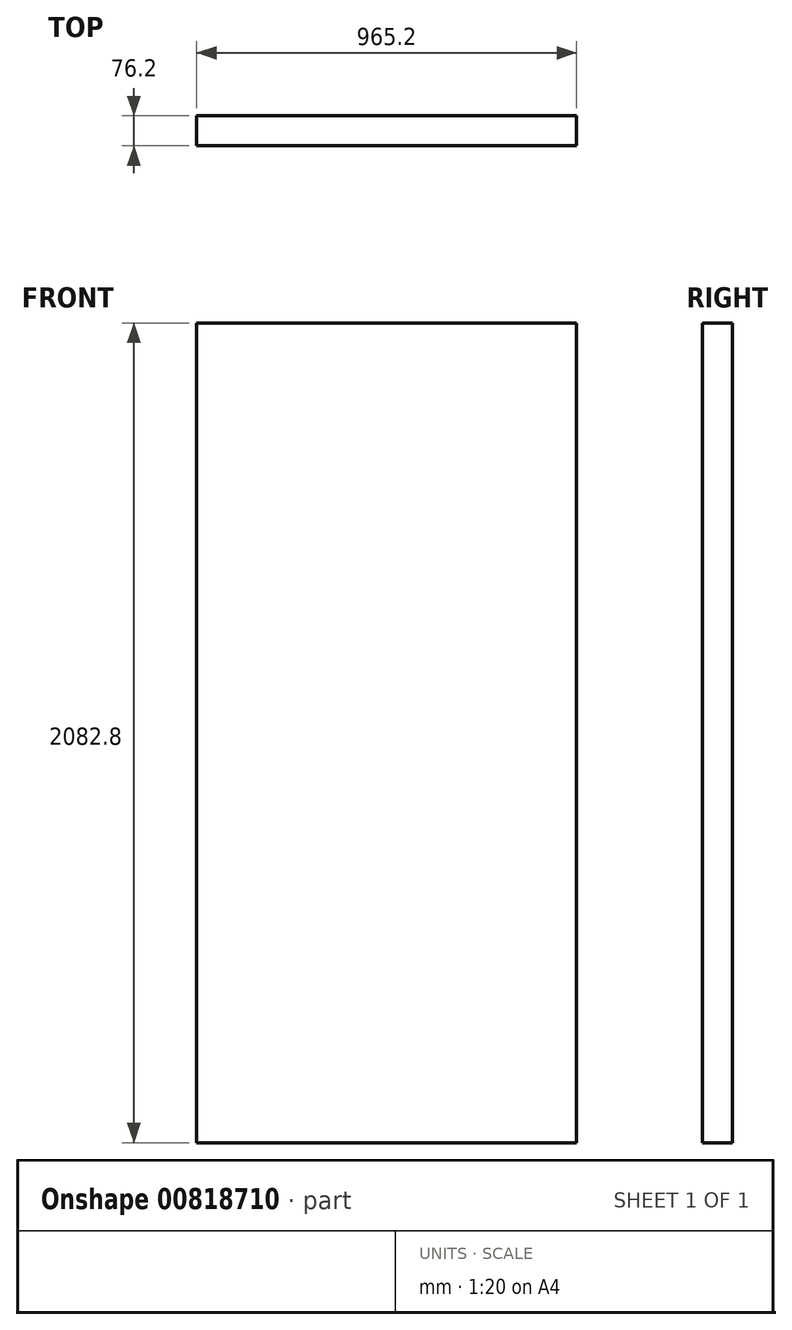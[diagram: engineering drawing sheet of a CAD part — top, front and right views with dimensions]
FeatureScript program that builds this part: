
annotation { "Feature Type Name" : "Feature", "Feature Type Description" : "" }
export const myFeature = defineFeature(function(context is Context, id is Id, definition is map)
    precondition{}
    {
        {
            var Q0;
            Q0=qCreatedBy(makeId("Front.planeOp"), FACE);
            var sketch = newSketch(context, id + "F0", { "sketchPlane" : qUnion([Q0])});
            skLineSegment(sketch, "E0.bottom", {"start": v(965.2, 2082.8) * mm, "end": v(0, 2082.8) * mm});
            skLineSegment(sketch, "E0.top", {"start": v(965.2, 0) * mm, "end": v(0, 0) * mm});
            skLineSegment(sketch, "E0.left", {"start": v(965.2, 2082.8) * mm, "end": v(965.2, 0) * mm});
            skLineSegment(sketch, "E0.right", {"start": v(0, 2082.8) * mm, "end": v(0, 0) * mm});
            skSolve(sketch);
        }
        {
            var Q0;
            Q0 = qSketchRegion(id + "F0", true);
            extrude(context, id + "F1", {"entities" : qUnion([Q0]), "domain" : OperationDomain.MODEL, "flatOperationType" : FlatOperationType.REMOVE, "depth" : 76.2 * mm, "offsetDistance" : 25.4 * mm});
        }
    });
